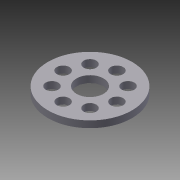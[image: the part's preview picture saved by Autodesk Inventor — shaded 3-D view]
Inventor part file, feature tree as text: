
AUTODESK INVENTOR PART (.ipt)
format: ipt  version: 2014 SP2 (Build 180246200, 246)  size: 252,416 bytes
history: native  units: in
note: dims shown in document units (in); Inventor stores cm internally (conversion verified against a paired STEP export)
features: other x1, extrude x1, imported_body x1, sketch x1
ambient origin geometry x8: Origin, YZ Plane, XZ Plane, XY Plane, X Axis, Y Axis, Z Axis, Center Point
bodies: Solid1 (feature_tree)
feature tree (4):
  other  "Large Flat Plate (Flowers).sat1"
  extrude  "Extrusion1"  Depth=0.3937in TaperAngle=0.0deg
  imported_body  "Base1"
  sketch  "Sketch1"  dims[d0=0.9843in d1=0.3937in d2=0.0in]
